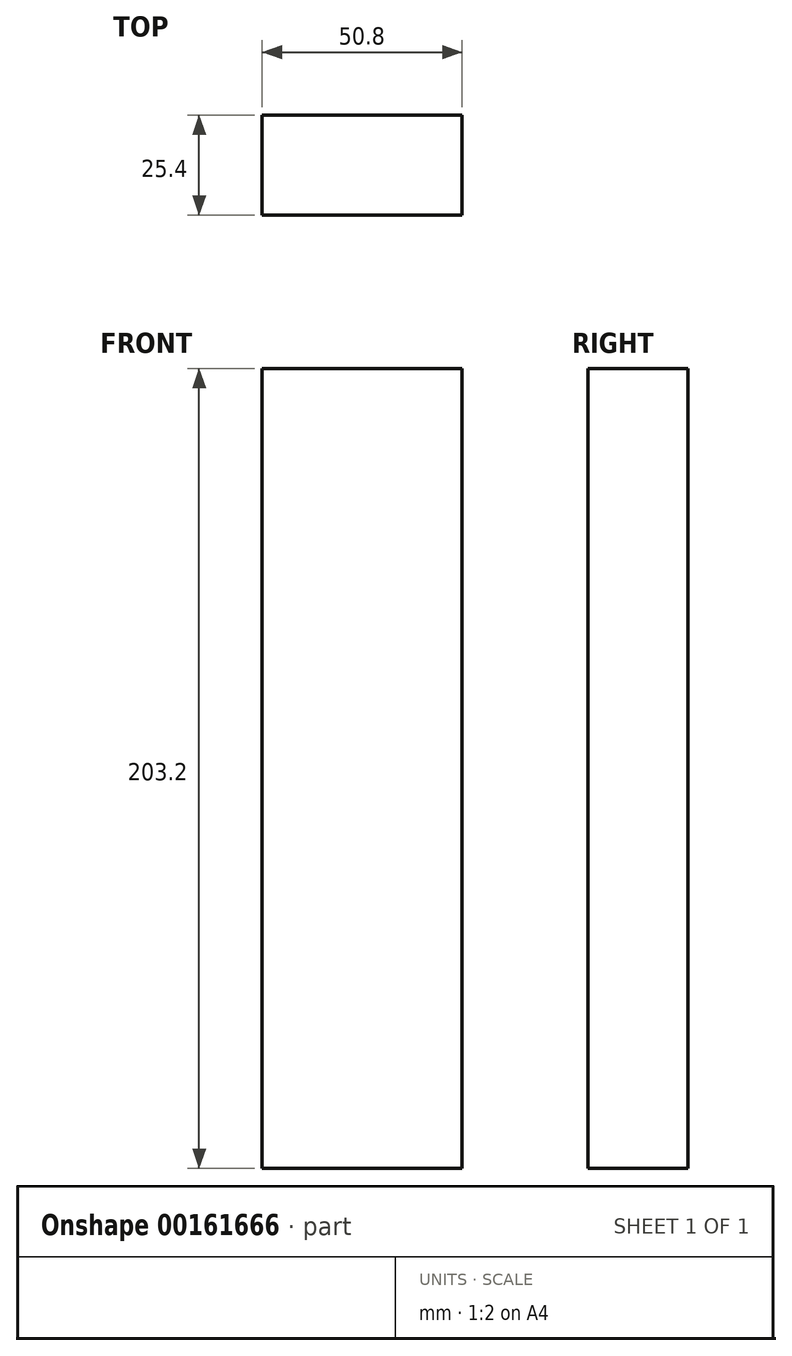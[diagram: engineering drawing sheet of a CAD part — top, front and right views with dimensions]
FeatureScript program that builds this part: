
annotation { "Feature Type Name" : "Feature", "Feature Type Description" : "" }
export const myFeature = defineFeature(function(context is Context, id is Id, definition is map)
    precondition{}
    {
        {
            var Q0;
            Q0=qCreatedBy(makeId("Front.planeOp"),FACE);
            var sketch = newSketch(context, id + "F0", { "sketchPlane" : qUnion([Q0])});
            skLineSegment(sketch, "E0.bottom", {"start": v(-58.75, 102.05) * mm, "end": v(-7.95, 102.05) * mm});
            skLineSegment(sketch, "E0.top", {"start": v(-58.75, -101.15) * mm, "end": v(-7.95, -101.15) * mm});
            skLineSegment(sketch, "E0.left", {"start": v(-58.75, 102.05) * mm, "end": v(-58.75, -101.15) * mm});
            skLineSegment(sketch, "E0.right", {"start": v(-7.95, 102.05) * mm, "end": v(-7.95, -101.15) * mm});
            skSolve(sketch);
        }
        {
            var Q0;
            Q0 = qSketchRegion(id + "F0", true);
            extrude(context, id + "F1", {"entities" : qUnion([Q0]), "depth" : 25.4 * mm});
        }
    });
